# Revit family: KLS - cupboard
name_source: partatom
category: Generic Models
revit_build: Autodesk Revit 2014 (Build: 20130308_1515(x64)
units: mm (PartAtom-declared; Revit-internal decimal feet)

## types (10) — shared parameters
Default Elevation = 1219 mm
distance to hole = 30 mm  [stored 0.0984252 ft]
handle = 50 mm  [stored 0.164042 ft]
handle distance = 100 mm  [stored 0.328084 ft]
handle radius = 25 mm  [stored 0.082021 ft]
hole = 30 mm  [stored 0.0984252 ft]
material wood_door = KLS - Walnut
material_handle = <By Category>
materialwood_cupboard = <By Category>
width = 1000 mm  [stored 3.28084 ft]

## per-type parameters (varying)
| type | handle height | height of cupboard | length of cupboard |
| KLS - cupboard_39cmx60cm | 195 mm  [stored 0.639764 ft] | 390 mm  [stored 1.27953 ft] | 600 mm |
| KLS - cupboard_54cmx60cm | 270 mm  [stored 0.885827 ft] | 540 mm  [stored 1.77165 ft] | 600 mm |
| KLS - cupboard_69cmx60cm | 345 mm  [stored 1.13189 ft] | 690 mm  [stored 2.26378 ft] | 600 mm |
| KLS - cupboard_84cmx60cm | 420 mm  [stored 1.37795 ft] | 840 mm  [stored 2.75591 ft] | 600 mm |
| KLS - cupboard_99cmx60cm | 495 mm  [stored 1.62402 ft] | 990 mm  [stored 3.24803 ft] | 600 mm |
| KLS - cupboard_99cmx80cm | 495 mm  [stored 1.62402 ft] | 990 mm  [stored 3.24803 ft] | 800 mm  [stored 2.62467 ft] |
| KLS - cupboard_84cmx80cm | 420 mm  [stored 1.37795 ft] | 840 mm  [stored 2.75591 ft] | 800 mm  [stored 2.62467 ft] |
| KLS - cupboard_69cmx80cm | 345 mm  [stored 1.13189 ft] | 690 mm  [stored 2.26378 ft] | 800 mm  [stored 2.62467 ft] |
| KLS - cupboard_54cmx80cm | 270 mm  [stored 0.885827 ft] | 540 mm  [stored 1.77165 ft] | 800 mm  [stored 2.62467 ft] |
| KLS - cupboard_39cmx80cm | 195 mm  [stored 0.639764 ft] | 390 mm  [stored 1.27953 ft] | 800 mm  [stored 2.62467 ft] |

note: [stored X ft] marks values corroborated as IEEE doubles in the binary element streams (Revit-internal decimal feet)

## geometry (parser evidence)
native form markers: Sweep x1
no freeform markers — native parametric forms only
